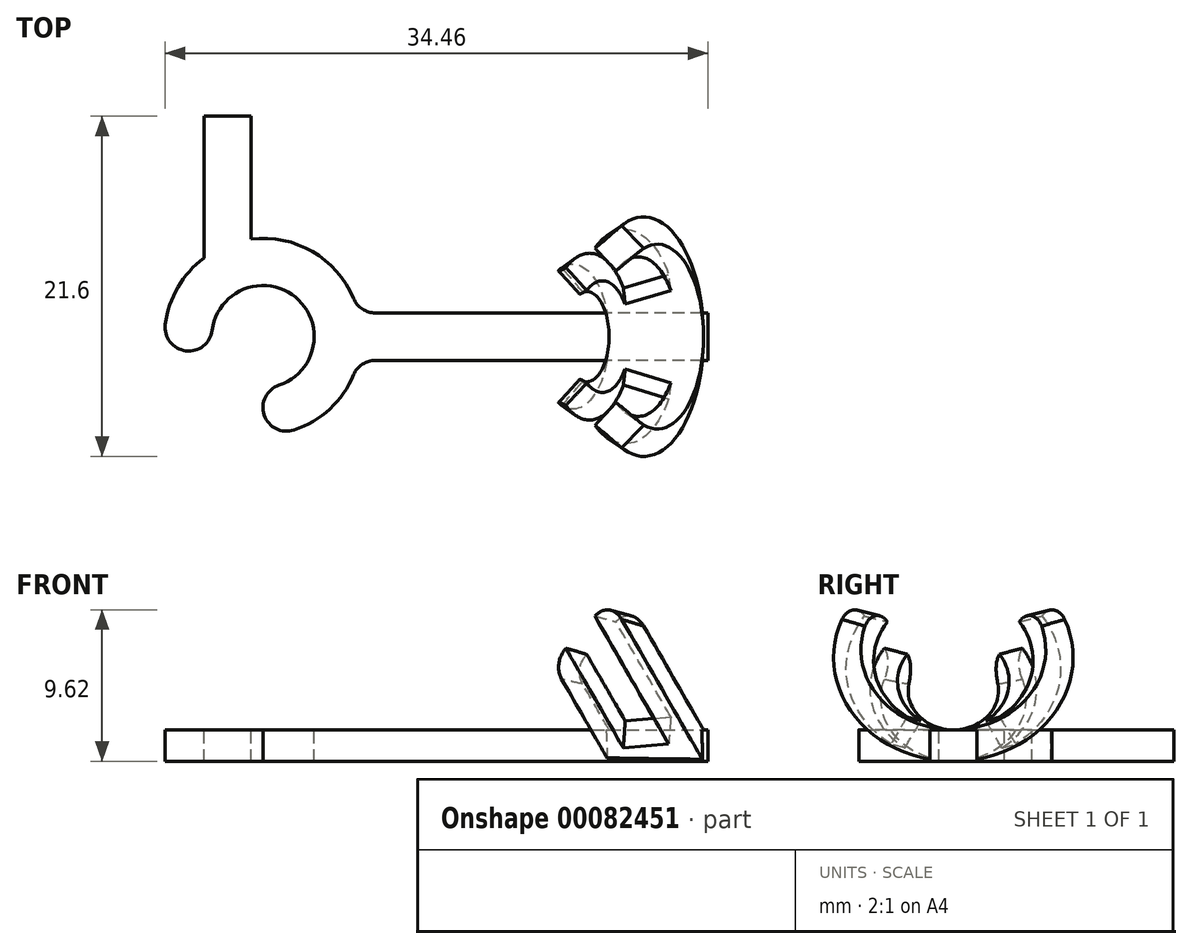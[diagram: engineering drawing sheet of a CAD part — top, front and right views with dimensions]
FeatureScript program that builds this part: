
annotation { "Feature Type Name" : "Feature", "Feature Type Description" : "" }
export const myFeature = defineFeature(function(context is Context, id is Id, definition is map)
    precondition{}
    {
        {
            var Q0;
            Q0=qCreatedBy(makeId("Top.planeOp"),FACE);
            var sketch = newSketch(context, id + "F0", { "sketchPlane" : qUnion([Q0])});
            skLineSegment(sketch, "E0.bottom", {"start": v(-25, 1.5) * mm, "end": v(0, 1.5) * mm});
            skLineSegment(sketch, "E0.top", {"start": v(-25, -1.5) * mm, "end": v(0, -1.5) * mm});
            skLineSegment(sketch, "E0.left", {"start": v(-25, 1.5) * mm, "end": v(-25, -1.5) * mm});
            skLineSegment(sketch, "E0.right", {"start": v(0, 1.5) * mm, "end": v(0, -1.5) * mm});
            skLineSegment(sketch, "E1.bottom", {"start": v(-32, 4.5) * mm, "end": v(-29, 4.5) * mm});
            skLineSegment(sketch, "E1.top", {"start": v(-32, 14) * mm, "end": v(-29, 14) * mm});
            skLineSegment(sketch, "E1.left", {"start": v(-32, 4.5) * mm, "end": v(-32, 14) * mm});
            skLineSegment(sketch, "E1.right", {"start": v(-29, 4.5) * mm, "end": v(-29, 14) * mm});
            skSolve(sketch);
        }
        {
            var Q0;
            Q0=makeQuery(id+"F0.imprint","IMPRINT",FACE,{"disambiguationData":[TD([[makeQuery(id+"F0.imprint","IMPRINT",EDGE,{"derivedFrom":sQuery(id+"F0.wireOp",EDGE,"E1.bottom")}),1.0]])]});
            extrude(context, id + "F1", {"entities" : qUnion([Q0]), "depth" : 2 * mm});
        }
        {
            var Q0;
            Q0=makeQuery(id+"F0.imprint","IMPRINT",FACE,{"disambiguationData":[TD([[makeQuery(id+"F0.imprint","IMPRINT",EDGE,{"derivedFrom":sQuery(id+"F0.wireOp",EDGE,"E0.bottom")}),-1.0]])]});
            extrude(context, id + "F2", {"entities" : qUnion([Q0]), "depth" : 2 * mm});
        }
        {
            var Q0;
            Q0=qCreatedBy(makeId("Front.planeOp"),FACE);
            var sketch = newSketch(context, id + "F3", { "sketchPlane" : qUnion([Q0])});
            skLineSegment(sketch, "E2.bottom", {"start": v(-25, 0) * mm, "end": v(-22, 0) * mm});
            skLineSegment(sketch, "E2.top", {"start": v(-25, 2) * mm, "end": v(-22, 2) * mm});
            skLineSegment(sketch, "E2.left", {"start": v(-25, 0) * mm, "end": v(-25, 2) * mm});
            skLineSegment(sketch, "E2.right", {"start": v(-22, 0) * mm, "end": v(-22, 2) * mm});
            skLineSegment(sketch, "E3", {"start": v(-28.25, 3.51) * mm, "end": v(-28.25, -2.02) * mm});
            skSolve(sketch);
        }
        {
            var Q0;
            Q0 = qSketchRegion(id + "F3", true);
            var Q1;
            Q1=sQuery(id+"F3.wireOp",EDGE,"E3");
            revolve(context, id + "F4", {"operationType" : NewBodyOperationType.ADD, "entities" : qUnion([Q0]), "axis" : qUnion([Q1]), "revolveType" : RevolveType.TWO_DIRECTIONS, "angle" : 90 * degree, "angleBack" : 168.74 * degree});
        }
        {
            var Q0;
            Q0=qCreatedBy(makeId("Front.planeOp"),FACE);
            var sketch = newSketch(context, id + "F5", { "sketchPlane" : qUnion([Q0])});
            skLineSegment(sketch, "E4.bottom", {"start": v(-6.27, 0) * mm, "end": v(-0.27, 0) * mm});
            skLineSegment(sketch, "E4.top", {"start": v(-6.27, 2) * mm, "end": v(-0.27, 2) * mm});
            skLineSegment(sketch, "E4.left", {"start": v(-6.27, 0) * mm, "end": v(-6.27, 2) * mm});
            skLineSegment(sketch, "E4.right", {"start": v(-0.27, 0) * mm, "end": v(-0.27, 2) * mm});
            skLineSegment(sketch, "E5", {"start": v(-7.85, 4.4) * mm, "end": v(0.08, 8.98) * mm});
            skSolve(sketch);
        }
        {
            var Q0;
            Q0 = qSketchRegion(id + "F5", true);
            var Q1;
            Q1=sQuery(id+"F5.wireOp",EDGE,"E5");
            revolve(context, id + "F6", {"operationType" : NewBodyOperationType.ADD, "entities" : qUnion([Q0]), "axis" : qUnion([Q1]), "revolveType" : RevolveType.SYMMETRIC, "angle" : 248.45 * degree});
        }
        {
            var Q0;
            Q0=makeQuery(id+"F6.opRevolve","CAP_EDGE",EDGE,{"disambiguationData":[OSD([sQuery(id+"F5.wireOp",EDGE,"E4.left")])],"isStart":false});
            var Q1;
            Q1=makeQuery(id+"F6.opRevolve","CAP_EDGE",EDGE,{"disambiguationData":[OSD([sQuery(id+"F5.wireOp",EDGE,"E4.right")])],"isStart":false});
            var Q2;
            Q2=makeQuery(id+"F6.opRevolve","CAP_EDGE",EDGE,{"disambiguationData":[OSD([sQuery(id+"F5.wireOp",EDGE,"E4.left")])],"isStart":true});
            var Q3;
            Q3=makeQuery(id+"F6.opRevolve","CAP_EDGE",EDGE,{"disambiguationData":[OSD([sQuery(id+"F5.wireOp",EDGE,"E4.right")])],"isStart":true});
            var Q4;
            Q4=makeQuery(id+"F4.boolean.opBoolean","INTERSECT",EDGE,{"derivedFrom":[makeQuery(id+"F2.opExtrude","SWEPT_FACE",FACE,{"disambiguationData":[OSD([sQuery(id+"F0.wireOp",EDGE,"E0.top")])]}),makeQuery(id+"F4.opRevolve","SWEPT_FACE",FACE,{"disambiguationData":[OSD([sQuery(id+"F3.wireOp",EDGE,"E2.right")])]})]});
            var Q5;
            Q5=makeQuery(id+"F4.opRevolve","CAP_EDGE",EDGE,{"disambiguationData":[OSD([sQuery(id+"F3.wireOp",EDGE,"E2.right")])],"isStart":false});
            var Q6;
            Q6=makeQuery(id+"F4.opRevolve","CAP_EDGE",EDGE,{"disambiguationData":[OSD([sQuery(id+"F3.wireOp",EDGE,"E2.left")])],"isStart":false});
            var Q7;
            Q7=makeQuery(id+"F4.opRevolve","CAP_EDGE",EDGE,{"disambiguationData":[OSD([sQuery(id+"F3.wireOp",EDGE,"E2.right")])],"isStart":true});
            var Q8;
            Q8=makeQuery(id+"F4.opRevolve","CAP_EDGE",EDGE,{"disambiguationData":[OSD([sQuery(id+"F3.wireOp",EDGE,"E2.left")])],"isStart":true});
            var Q9;
            Q9=makeQuery(id+"F4.boolean.opBoolean","INTERSECT",EDGE,{"derivedFrom":[makeQuery(id+"F2.opExtrude","SWEPT_FACE",FACE,{"disambiguationData":[OSD([sQuery(id+"F0.wireOp",EDGE,"E0.bottom")])]}),makeQuery(id+"F4.opRevolve","SWEPT_FACE",FACE,{"disambiguationData":[OSD([sQuery(id+"F3.wireOp",EDGE,"E2.right")])]})]});
            fillet(context, id + "F7", {"entities" : qUnion([Q0, Q1, Q2, Q3, Q4, Q5, Q6, Q7, Q8, Q9]), "radius" : 1.5 * mm, "tangentPropagation" : true, "allowEdgeOverflow" : false});
        }
        {
            var Q0;
            Q0=makeQuery(id+"F6.opRevolve","CAP_FACE",FACE,{"disambiguationData":[OSD([sQuery(id+"F5.wireOp",EDGE,"E4.bottom"),sQuery(id+"F5.wireOp",EDGE,"E4.top"),sQuery(id+"F5.wireOp",EDGE,"E4.left"),sQuery(id+"F5.wireOp",EDGE,"E4.right")])],"isStart":false});
            var Q1;
            Q1=makeQuery(id+"F6.opRevolve","CAP_FACE",FACE,{"disambiguationData":[OSD([sQuery(id+"F5.wireOp",EDGE,"E4.bottom"),sQuery(id+"F5.wireOp",EDGE,"E4.top"),sQuery(id+"F5.wireOp",EDGE,"E4.left"),sQuery(id+"F5.wireOp",EDGE,"E4.right")])],"isStart":true});
            var Q2;
            Q2=sQuery(id+"F5.wireOp",EDGE,"E5");
            revolve(context, id + "F8", {"operationType" : NewBodyOperationType.REMOVE, "entities" : qUnion([Q0, Q1]), "axis" : qUnion([Q2]), "revolveType" : RevolveType.SYMMETRIC, "oppositeDirection" : true, "angle" : 177.46 * degree});
        }
    });
